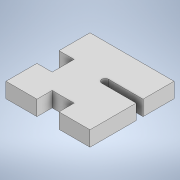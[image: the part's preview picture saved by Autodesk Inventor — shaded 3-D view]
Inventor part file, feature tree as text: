
AUTODESK INVENTOR PART (.ipt)
format: ipt  version: 2020 (Build 240168000, 168)  size: 116,224 bytes
history: native  units: mm
features: extrude x1, sketch x1
ambient origin geometry x8: Origin, YZ Plane, XZ Plane, XY Plane, X Axis, Y Axis, Z Axis, Center Point
bodies: Solide1 (feature_tree)
feature tree (2):
  extrude  "Extrusion1"  Depth=122.0mm
  sketch  "Esquisse1"
